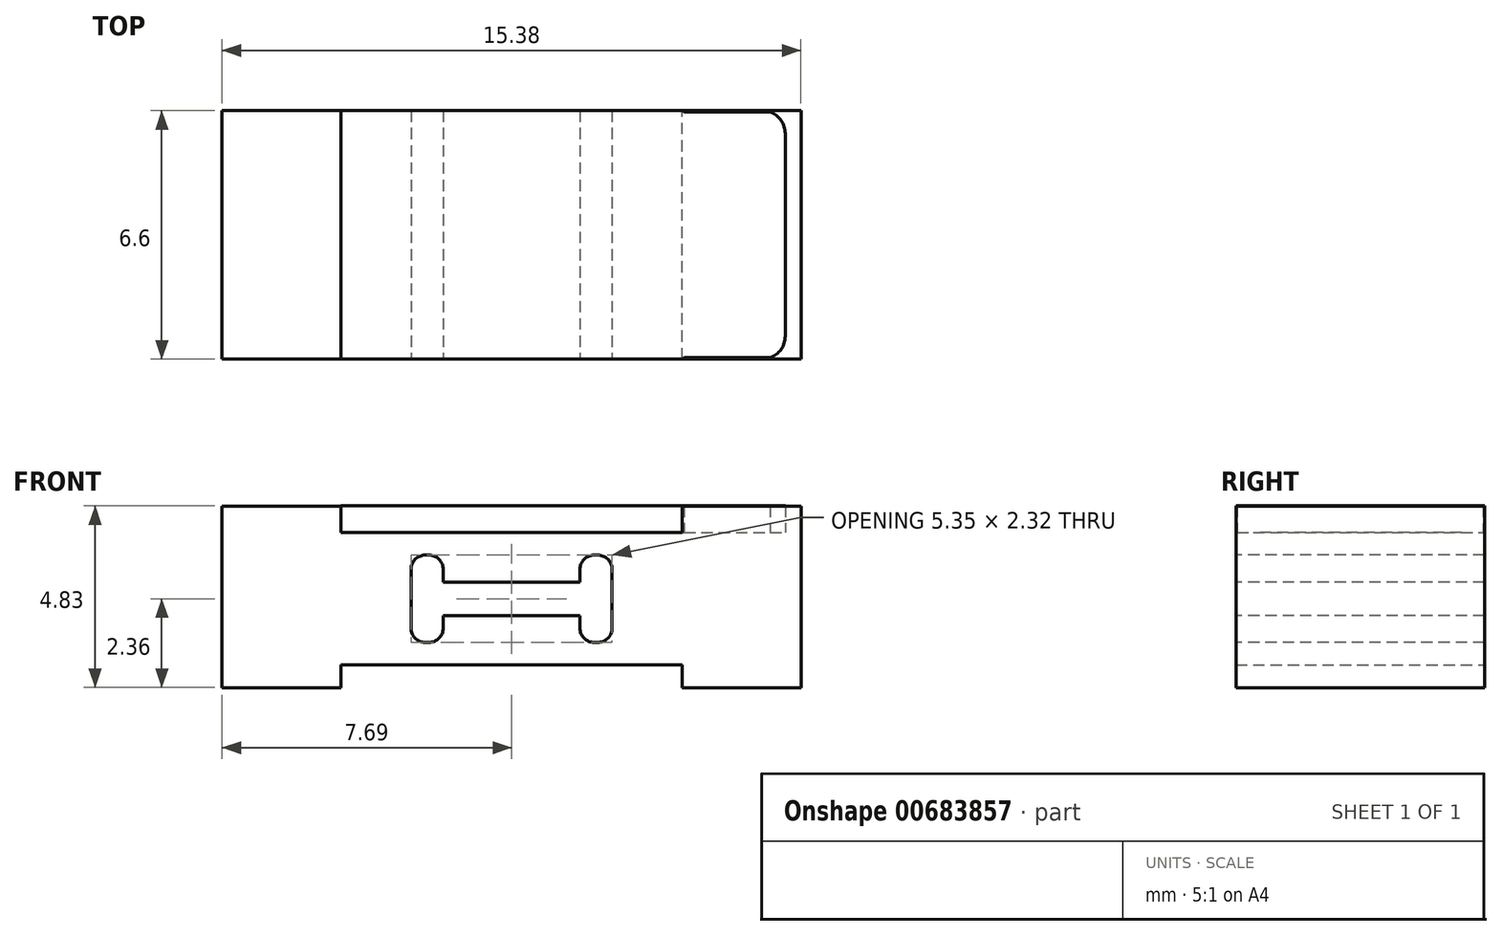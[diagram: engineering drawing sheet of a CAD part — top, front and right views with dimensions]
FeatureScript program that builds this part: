
annotation { "Feature Type Name" : "Feature", "Feature Type Description" : "" }
export const myFeature = defineFeature(function(context is Context, id is Id, definition is map)
    precondition{}
    {
        {
            var Q0;
            Q0=qCreatedBy(makeId("Front.planeOp"),FACE);
            var sketch = newSketch(context, id + "F0", { "sketchPlane" : qUnion([Q0])});
            skLineSegment(sketch, "E0.bottom", {"start": v(4.54, -1.76) * mm, "end": v(-4.54, -1.76) * mm});
            skLineSegment(sketch, "E0.top", {"start": v(4.54, 1.76) * mm, "end": v(-4.54, 1.76) * mm});
            skLineSegment(sketch, "E0.left", {"start": v(4.54, -1.76) * mm, "end": v(4.54, 1.76) * mm});
            skLineSegment(sketch, "E0.right", {"start": v(-4.54, -1.76) * mm, "end": v(-4.54, 1.76) * mm});
            skPoint(sketch, "E0.middle", {"position": v(0, 0) * mm});
            skLineSegment(sketch, "E1.bottom", {"start": v(-4.54, 2.46) * mm, "end": v(-7.7, 2.46) * mm});
            skLineSegment(sketch, "E1.top", {"start": v(-4.54, -2.36) * mm, "end": v(-7.7, -2.36) * mm});
            skLineSegment(sketch, "E1.left", {"start": v(-4.54, 2.46) * mm, "end": v(-4.54, -2.36) * mm});
            skLineSegment(sketch, "E1.right", {"start": v(-7.7, 2.46) * mm, "end": v(-7.7, -2.36) * mm});
            skLineSegment(sketch, "E2.MirrorCS", {"start": v(4.54, 2.46) * mm, "end": v(4.54, -2.36) * mm});
            skLineSegment(sketch, "E3.MirrorCS", {"start": v(4.54, 2.46) * mm, "end": v(7.7, 2.46) * mm});
            skLineSegment(sketch, "E4.MirrorCS", {"start": v(7.7, 2.46) * mm, "end": v(7.7, -2.36) * mm});
            skLineSegment(sketch, "E5.MirrorCS", {"start": v(4.54, -2.36) * mm, "end": v(7.7, -2.36) * mm});
            skLineSegment(sketch, "E6.bottom", {"start": v(-7.5, -3.17) * mm, "end": v(-7.55, -3.17) * mm});
            skLineSegment(sketch, "E6.top", {"start": v(-7.5, 3.17) * mm, "end": v(-7.55, 3.17) * mm});
            skPoint(sketch, "E6.middle", {"position": v(-7.52, 0) * mm});
            skPoint(sketch, "E7.visualSharp", {"position": v(-9.25, 3.17) * mm});
            skPoint(sketch, "E8.visualSharp", {"position": v(-5.8, 3.17) * mm});
            skPoint(sketch, "E9.visualSharp", {"position": v(-9.25, -3.17) * mm});
            skPoint(sketch, "E10.visualSharp", {"position": v(-5.8, -3.17) * mm});
            skSolve(sketch);
        }
        {
            var Q0;
            Q0 = qSketchRegion(id + "F0", true);
            extrude(context, id + "F1", {"entities" : qUnion([Q0]), "depth" : 3.3 * mm, "offsetDistance" : 25.4 * mm, "hasSecondDirection" : true, "secondDirectionOppositeDirection" : true, "secondDirectionDepth" : 3.3 * mm});
        }
        {
            var Q0;
            Q0=makeQuery(id+"F1.opExtrude","CAP_FACE",FACE,{"disambiguationData":[OSD([sQuery(id+"F0.wireOp",EDGE,"E0.bottom"),sQuery(id+"F0.wireOp",EDGE,"E0.top"),sQuery(id+"F0.wireOp",EDGE,"E1.bottom"),sQuery(id+"F0.wireOp",EDGE,"E1.top"),sQuery(id+"F0.wireOp",EDGE,"E1.left"),sQuery(id+"F0.wireOp",EDGE,"E1.right"),sQuery(id+"F0.wireOp",EDGE,"E2.MirrorCS"),sQuery(id+"F0.wireOp",EDGE,"E3.MirrorCS"),sQuery(id+"F0.wireOp",EDGE,"E4.MirrorCS"),sQuery(id+"F0.wireOp",EDGE,"E5.MirrorCS")])],"isStart":false});
            var sketch = newSketch(context, id + "F2", { "sketchPlane" : qUnion([Q0])});
            skLineSegment(sketch, "E11.bottom", {"start": v(1.82, -0.44) * mm, "end": v(-1.82, -0.44) * mm});
            skLineSegment(sketch, "E11.top", {"start": v(1.82, 0.44) * mm, "end": v(-1.82, 0.44) * mm});
            skLineSegment(sketch, "E11.left", {"start": v(1.82, -0.44) * mm, "end": v(1.82, 0.44) * mm});
            skLineSegment(sketch, "E11.right", {"start": v(-1.82, -0.44) * mm, "end": v(-1.82, 0.44) * mm});
            skPoint(sketch, "E11.middle", {"position": v(0, 0) * mm});
            skLineSegment(sketch, "E12.bottom", {"start": v(2.3, -1.16) * mm, "end": v(2.2, -1.16) * mm});
            skLineSegment(sketch, "E12.top", {"start": v(2.3, 1.16) * mm, "end": v(2.2, 1.16) * mm});
            skLineSegment(sketch, "E12.left", {"start": v(2.67, -0.78) * mm, "end": v(2.67, 0.78) * mm});
            skLineSegment(sketch, "E12.right", {"start": v(1.82, -0.78) * mm, "end": v(1.82, 0.78) * mm});
            skPoint(sketch, "E12.middle", {"position": v(2.24, 0) * mm});
            skLineSegment(sketch, "E13.MirrorCS", {"start": v(-1.82, -0.78) * mm, "end": v(-1.82, 0.78) * mm});
            skLineSegment(sketch, "E14.MirrorCS", {"start": v(-2.3, -1.16) * mm, "end": v(-2.2, -1.16) * mm});
            skLineSegment(sketch, "E15.MirrorCS", {"start": v(-2.67, -0.78) * mm, "end": v(-2.67, 0.78) * mm});
            skLineSegment(sketch, "E16.MirrorCS", {"start": v(-2.3, 1.16) * mm, "end": v(-2.2, 1.16) * mm});
            skPoint(sketch, "E17.visualSharp", {"position": v(-2.67, 1.16) * mm});
            skArc(sketch, "E17.filletArc", {"start": v(-2.3, 1.16) * mm, "mid": v(-2.56, 1.05) * mm, "end": v(-2.67, 0.78) * mm});
            skPoint(sketch, "E18.visualSharp", {"position": v(-1.82, 1.16) * mm});
            skArc(sketch, "E18.filletArc", {"start": v(-1.82, 0.78) * mm, "mid": v(-1.93, 1.05) * mm, "end": v(-2.2, 1.16) * mm});
            skPoint(sketch, "E19.visualSharp", {"position": v(-2.67, -1.16) * mm});
            skArc(sketch, "E19.filletArc", {"start": v(-2.67, -0.78) * mm, "mid": v(-2.56, -1.05) * mm, "end": v(-2.3, -1.16) * mm});
            skPoint(sketch, "E20.visualSharp", {"position": v(-1.82, -1.16) * mm});
            skArc(sketch, "E20.filletArc", {"start": v(-2.2, -1.16) * mm, "mid": v(-1.93, -1.05) * mm, "end": v(-1.82, -0.78) * mm});
            skPoint(sketch, "E21.visualSharp", {"position": v(1.82, 1.16) * mm});
            skArc(sketch, "E21.filletArc", {"start": v(2.2, 1.16) * mm, "mid": v(1.93, 1.05) * mm, "end": v(1.82, 0.78) * mm});
            skPoint(sketch, "E22.visualSharp", {"position": v(2.67, 1.16) * mm});
            skArc(sketch, "E22.filletArc", {"start": v(2.67, 0.78) * mm, "mid": v(2.56, 1.05) * mm, "end": v(2.3, 1.16) * mm});
            skPoint(sketch, "E23.visualSharp", {"position": v(2.67, -1.16) * mm});
            skArc(sketch, "E23.filletArc", {"start": v(2.3, -1.16) * mm, "mid": v(2.56, -1.05) * mm, "end": v(2.67, -0.78) * mm});
            skPoint(sketch, "E24.visualSharp", {"position": v(1.82, -1.16) * mm});
            skArc(sketch, "E24.filletArc", {"start": v(1.82, -0.78) * mm, "mid": v(1.93, -1.05) * mm, "end": v(2.2, -1.16) * mm});
            skSolve(sketch);
        }
        {
            var Q0;
            Q0 = qSketchRegion(id + "F2", true);
            extrude(context, id + "F3", {"entities" : qUnion([Q0]), "operationType" : NewBodyOperationType.REMOVE, "oppositeDirection" : true, "depth" : 6.8 * mm, "offsetDistance" : 25.4 * mm});
        }
        {
            var Q0;
            Q0=makeQuery(id+"F1.opExtrude","SWEPT_FACE",FACE,{"disambiguationData":[OSD([sQuery(id+"F0.wireOp",EDGE,"E0.top")])]});
            var sketch = newSketch(context, id + "F4", { "sketchPlane" : qUnion([Q0])});
            skLineSegment(sketch, "E25.bottom", {"start": v(-4.54, 3.3) * mm, "end": v(4.54, 3.3) * mm});
            skLineSegment(sketch, "E25.top", {"start": v(-4.54, -3.3) * mm, "end": v(6.66, -3.3) * mm});
            skLineSegment(sketch, "E25.left", {"start": v(-4.54, 3.3) * mm, "end": v(-4.54, -3.3) * mm});
            skLineSegment(sketch, "E25.right", {"start": v(7.27, 2.7) * mm, "end": v(7.27, -2.7) * mm});
            skPoint(sketch, "E26.visualSharp", {"position": v(7.27, 3.3) * mm});
            skArc(sketch, "E26.filletArc", {"start": v(7.27, 2.7) * mm, "mid": v(7.16, 3.04) * mm, "end": v(6.87, 3.27) * mm});
            skPoint(sketch, "E27.visualSharp", {"position": v(7.27, -3.3) * mm});
            skArc(sketch, "E27.filletArc", {"start": v(6.87, -3.27) * mm, "mid": v(7.16, -3.04) * mm, "end": v(7.27, -2.7) * mm});
            skLineSegment(sketch, "E28", {"start": v(4.54, 3.3) * mm, "end": v(4.59, 3.27) * mm});
            skLineSegment(sketch, "E29", {"start": v(4.59, 3.27) * mm, "end": v(6.87, 3.27) * mm});
            skLineSegment(sketch, "E30.MirrorCS", {"start": v(4.59, -3.27) * mm, "end": v(6.87, -3.27) * mm});
            skLineSegment(sketch, "E31.MirrorCS", {"start": v(4.54, -3.3) * mm, "end": v(4.59, -3.27) * mm});
            skSolve(sketch);
        }
        {
            var Q0;
            Q0 = qSketchRegion(id + "F4", true);
            extrude(context, id + "F5", {"entities" : qUnion([Q0]), "depth" : 0.71 * mm, "offsetDistance" : 25.4 * mm});
        }
    });
